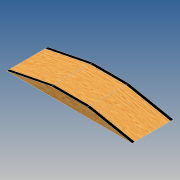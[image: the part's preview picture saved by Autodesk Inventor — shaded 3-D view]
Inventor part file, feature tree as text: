
AUTODESK INVENTOR PART (.ipt)
format: ipt  version: 2020 (Build 240168000, 168)  size: 177,664 bytes
history: native  units: mm
features: extrude x6, sketch x6
ambient origin geometry x8: Origin, YZ Plane, XZ Plane, XY Plane, X Axis, Y Axis, Z Axis, Center Point
bodies: Solid1 (feature_tree)
feature tree (12):
  extrude  "Extrusion1"  Depth=100.0mm
  extrude  "Extrusion2"  Depth=460.0mm
  extrude  "Extrusion3"  Depth=30.0mm
  extrude  "Extrusion4"  Depth=0.5mm TaperAngle=0.0deg
  extrude  "Extrusion5"  Depth=510.344311mm
  extrude  "Extrusion6"  Depth=0.5mm TaperAngle=0.0deg
  sketch  "Sketch1"  dims[d0=400.0mm d1=100.0mm]
  sketch  "Sketch2"  dims[d4=460.0mm d5=0.0mm d6=1.972222mm]
  sketch  "Sketch3"  dims[d7=29.443704mm d8=30.0mm]
  sketch  "Sketch4"  dims[d9=30.0mm d10=0.5mm d11=0.0mm]
  sketch  "Sketch5"  dims[d12=30.0mm d13=510.344311mm]
  sketch  "Sketch6"  dims[d14=30.0mm d15=0.5mm d16=0.0mm d17=30.0mm d18=30.0mm d19=0.5mm d20=0.0mm d21=460.0mm d22=0.0mm d23=460.0mm d24=0.0mm]
